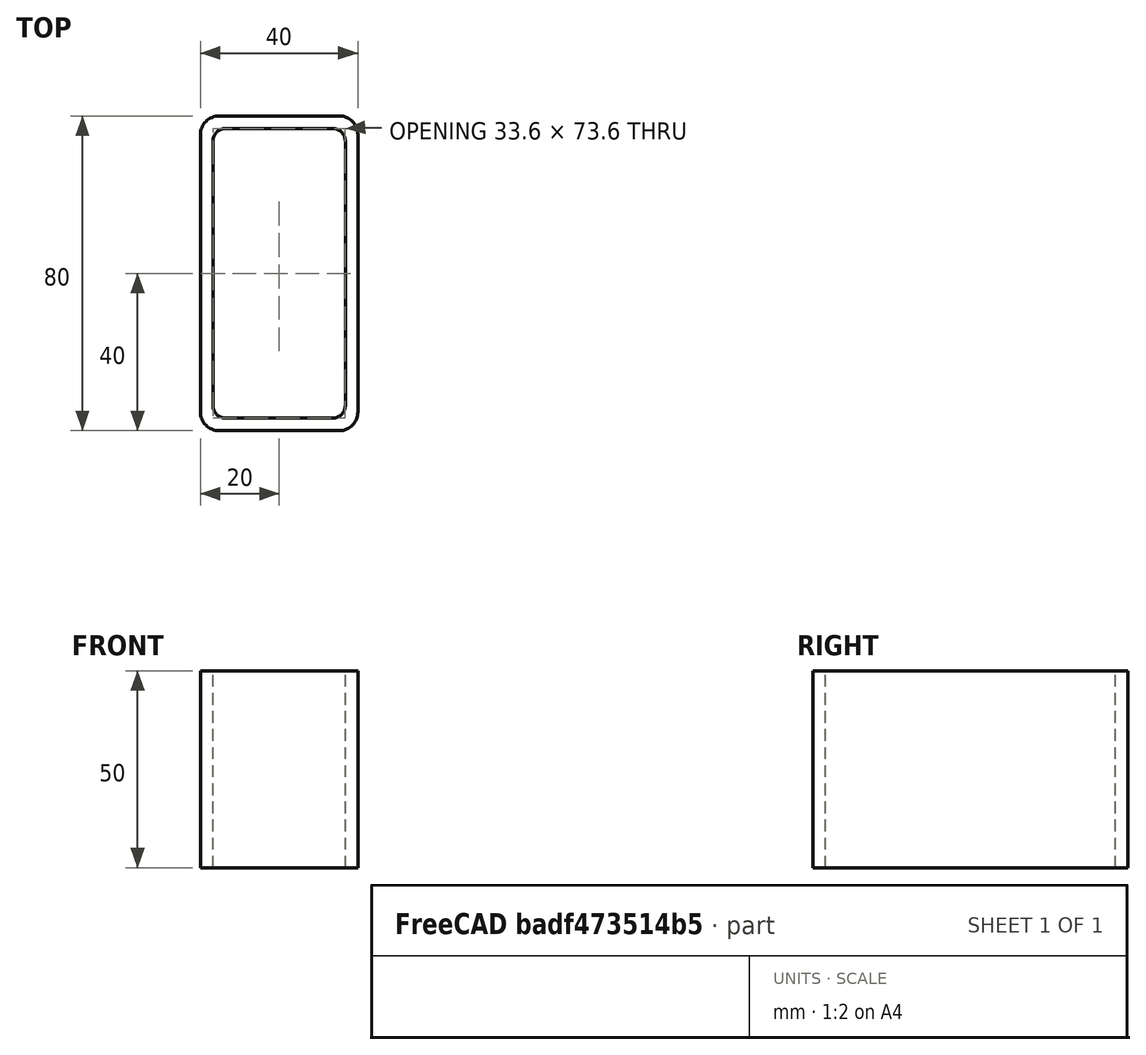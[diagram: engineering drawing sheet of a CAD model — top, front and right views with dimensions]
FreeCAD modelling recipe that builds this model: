
FCSTD DOCUMENT  (FreeCAD 0.15R4671 (Git))
Label: Rectangular hollow section 80x40x3.2 EN10219 S235JRH
License: All rights reserved
LicenseURL: http://en.wikipedia.org/wiki/All_rights_reserved
objects: Sketcher::SketchObject×1, Part::Extrusion×1
note: 2 computed .brp shape members not serialized (recipe doc carries the construction recipe); baked Part::Feature solids carry a one-line shape summary decoded from their .brp

FEATURE [Sketcher::SketchObject] Sketch
  sketch-geometry (16):
    g0: LineSegment StartX=-13.6 StartY=36.8 StartZ=0 EndX=13.6 EndY=36.8 EndZ=0
    g1: LineSegment StartX=16.8 StartY=33.6 StartZ=0 EndX=16.8 EndY=-33.6 EndZ=0
    g2: LineSegment StartX=13.6 StartY=-36.8 StartZ=0 EndX=-13.6 EndY=-36.8 EndZ=0
    g3: LineSegment StartX=-16.8 StartY=-33.6 StartZ=0 EndX=-16.8 EndY=33.6 EndZ=0
    g4: LineSegment StartX=-15.2 StartY=40 StartZ=0 EndX=15.2 EndY=40 EndZ=0
    g5: LineSegment StartX=20 StartY=35.2 StartZ=0 EndX=20 EndY=-35.2 EndZ=0
    g6: LineSegment StartX=15.2 StartY=-40 StartZ=0 EndX=-15.2 EndY=-40 EndZ=0
    g7: LineSegment StartX=-20 StartY=-35.2 StartZ=0 EndX=-20 EndY=35.2 EndZ=0
    g8: ArcOfCircle CenterX=-13.6 CenterY=33.6 CenterZ=0 NormalX=0 NormalY=0 NormalZ=1 Radius=3.2 StartAngle=1.5708 EndAngle=3.14159
    g9: ArcOfCircle CenterX=13.6 CenterY=33.6 CenterZ=0 NormalX=0 NormalY=0 NormalZ=1 Radius=3.2 StartAngle=0 EndAngle=1.5708
    g10: ArcOfCircle CenterX=13.6 CenterY=-33.6 CenterZ=0 NormalX=0 NormalY=0 NormalZ=1 Radius=3.2 StartAngle=4.71239 EndAngle=6.28319
    g11: ArcOfCircle CenterX=-13.6 CenterY=-33.6 CenterZ=0 NormalX=0 NormalY=0 NormalZ=1 Radius=3.2 StartAngle=3.14159 EndAngle=4.71239
    g12: ArcOfCircle CenterX=15.2 CenterY=35.2 CenterZ=0 NormalX=0 NormalY=0 NormalZ=1 Radius=4.8 StartAngle=0 EndAngle=1.5708
    g13: ArcOfCircle CenterX=15.2 CenterY=-35.2 CenterZ=0 NormalX=0 NormalY=0 NormalZ=1 Radius=4.8 StartAngle=4.71239 EndAngle=6.28319
    g14: ArcOfCircle CenterX=-15.2 CenterY=-35.2 CenterZ=0 NormalX=0 NormalY=0 NormalZ=1 Radius=4.8 StartAngle=3.14159 EndAngle=4.71239
    g15: ArcOfCircle CenterX=-15.2 CenterY=35.2 CenterZ=0 NormalX=0 NormalY=0 NormalZ=1 Radius=4.8 StartAngle=1.5708 EndAngle=3.14159
  constraints (36):
    c: Horizontal(g2)
    c: Vertical(g3)
    c: Horizontal(g6)
    c: Vertical(g7)
    c: Tangent(g3,g8) = 1.5708
    c: Tangent(g0,g8) = 1.5708
    c: Tangent(g0,g9) = 1.5708
    c: Tangent(g1,g9) = 1.5708
    c: Tangent(g1,g10) = 1.5708
    c: Tangent(g2,g10) = 1.5708
    c: Tangent(g2,g11) = 1.5708
    c: Tangent(g3,g11) = 1.5708
    c: Tangent(g4,g12) = 1.5708
    c: Tangent(g5,g12) = 1.5708
    c: Tangent(g5,g13) = 1.5708
    c: Tangent(g6,g13) = 1.5708
    c: Tangent(g6,g14) = 1.5708
    c: Tangent(g7,g14) = 1.5708
    c: Tangent(g7,g15) = 1.5708
    c: Tangent(g4,g15) = 1.5708
    c: Equal(g9,g8)
    c: Equal(g9,g11)
    c: Equal(g9,g10)
    c: Equal(g12,g15)
    c: Equal(g12,g14)
    c: Equal(g12,g13)
    c: Symmetric(g4,g6,g-1)
    c: Symmetric(g7,g5,g-2)
    c: DistanceY(g4,g6) = -80
    c: DistanceX(g7,g5) = 40
    c: Symmetric(g3,g1,g-2)
    c: Symmetric(g0,g2,g-1)
    c: DistanceY(g0,g4) = 3.2
    c: DistanceX(g5,g1) = -3.2
    c: Radius(g9) = 3.2
    c: Radius(g12) = 4.8
FEATURE [Part::Extrusion] Extrude  label="Rectangular hollow section 80x40x3.2 EN10219 S235JRH"
  Base = -> Sketch
  Dir = (0,0,50)
  Solid = true
